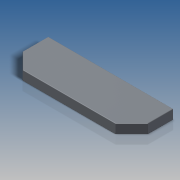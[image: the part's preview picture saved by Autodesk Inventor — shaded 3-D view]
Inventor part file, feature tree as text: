
AUTODESK INVENTOR PART (.ipt)
format: ipt  version: 2016 SP2 (Build 200236200, 236)  size: 121,344 bytes
history: native  units: in
note: dims shown in document units (in); Inventor stores cm internally (conversion verified against a paired STEP export)
features: extrude x1, fillet x1, sketch x1
ambient origin geometry x8: Origin, YZ Plane, XZ Plane, XY Plane, X Axis, Y Axis, Z Axis, Center Point
bodies: Solid1 (feature_tree)
feature tree (3):
  extrude  "Extrusion1"  Depth=0.8504in
  fillet  "Fillet1"  Radius=0.2835in
  sketch  "Sketch2"  dims[d0=0.6299in d1=0.8504in d2=0.2835in d3=0.063in d4=0.0in d5=0.0039in]
